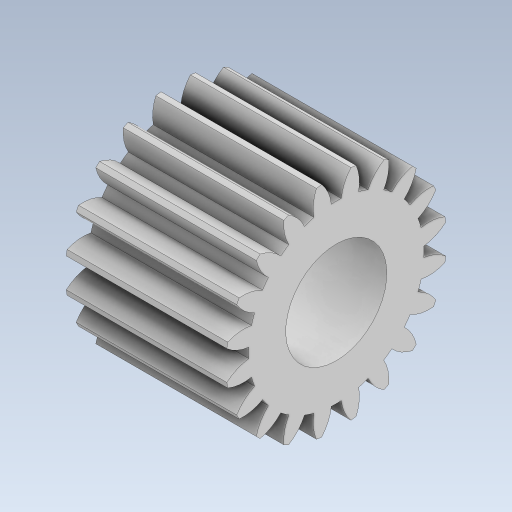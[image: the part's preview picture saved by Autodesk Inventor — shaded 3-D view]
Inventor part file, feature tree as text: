
AUTODESK INVENTOR PART (.ipt)
format: ipt  version: 2023 (Build 270158000, 158)  size: 292,864 bytes
history: native  units: in
note: dims shown in document units (in); Inventor stores cm internally (conversion verified against a paired STEP export)
features: extrude x2, sketch x2, other x1
ambient origin geometry x8: Origin, YZ Plane, XZ Plane, XY Plane, X Axis, Y Axis, Z Axis, Center Point
bodies: Solid1 (feature_tree)
feature tree (5):
  extrude  "Extrusion1"  TaperAngle=0.0deg  [1 undecoded]
  extrude  "Extrusion2"  TaperAngle=0.0deg  [1 undecoded]
  sketch  "Sketch1"  dims[d0=0.5in d1=0.0in d2=0.0in]
  sketch  "Sketch2"  dims[d4=0.315in d5=0.0in d6=0.0in]
  other  "TeethCuts"
note: 2 required parameter values undecoded (feature->parameter linkage not recoverable at this tier; creation-order binding heuristic only, values carry confidence <= 0.55)
